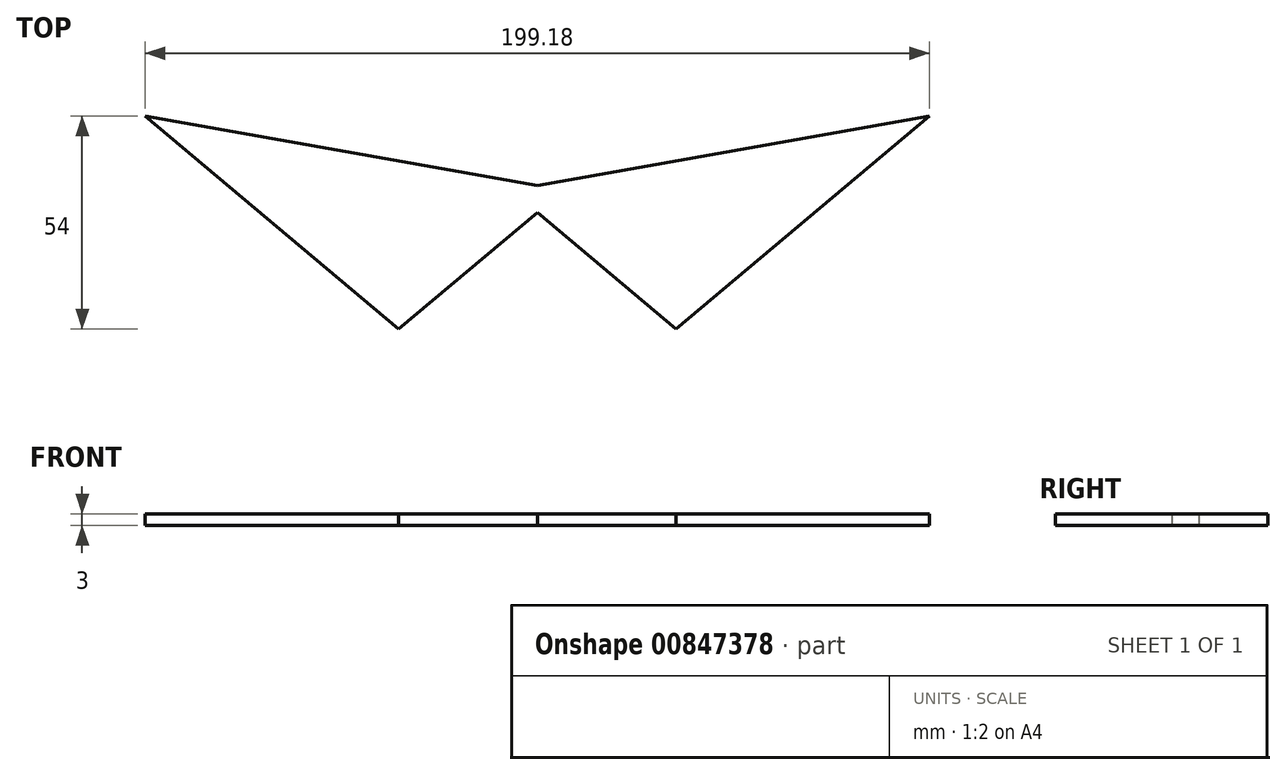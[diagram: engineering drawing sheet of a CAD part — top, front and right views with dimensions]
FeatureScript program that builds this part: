
annotation { "Feature Type Name" : "Feature", "Feature Type Description" : "" }
export const myFeature = defineFeature(function(context is Context, id is Id, definition is map)
    precondition{}
    {
        {
            var Q0;
            Q0=qCreatedBy(makeId("Top.planeOp"),FACE);
            var sketch = newSketch(context, id + "F0", { "sketchPlane" : qUnion([Q0])});
            skLineSegment(sketch, "E0", {"start": v(0, 0) * mm, "end": v(-35.24, -29.57) * mm});
            skLineSegment(sketch, "E1", {"start": v(-35.24, -29.57) * mm, "end": v(-99.59, 24.43) * mm});
            skLineSegment(sketch, "E2", {"start": v(-99.59, 24.43) * mm, "end": v(0, 6.87) * mm});
            skLineSegment(sketch, "E3.MirrorCS", {"start": v(35.24, -29.57) * mm, "end": v(99.59, 24.43) * mm});
            skLineSegment(sketch, "E4.MirrorCS", {"start": v(0, 0) * mm, "end": v(35.24, -29.57) * mm});
            skLineSegment(sketch, "E5.MirrorCS", {"start": v(99.59, 24.43) * mm, "end": v(0, 6.87) * mm});
            skPoint(sketch, "E6", {"position": v(-21.2, 10.6) * mm});
            skPoint(sketch, "E7", {"position": v(21.2, 10.6) * mm});
            skSolve(sketch);
        }
        {
            var Q0;
            Q0=makeQuery(id+"F0.imprint","IMPRINT",FACE,{"disambiguationData":[TD([[makeQuery(id+"F0.imprint","IMPRINT",EDGE,{"derivedFrom":sQuery(id+"F0.wireOp",EDGE,"E0")}),-1.0]])]});
            extrude(context, id + "F1", {"entities" : qUnion([Q0]), "depth" : 3 * mm, "offsetDistance" : 25 * mm});
        }
    });
